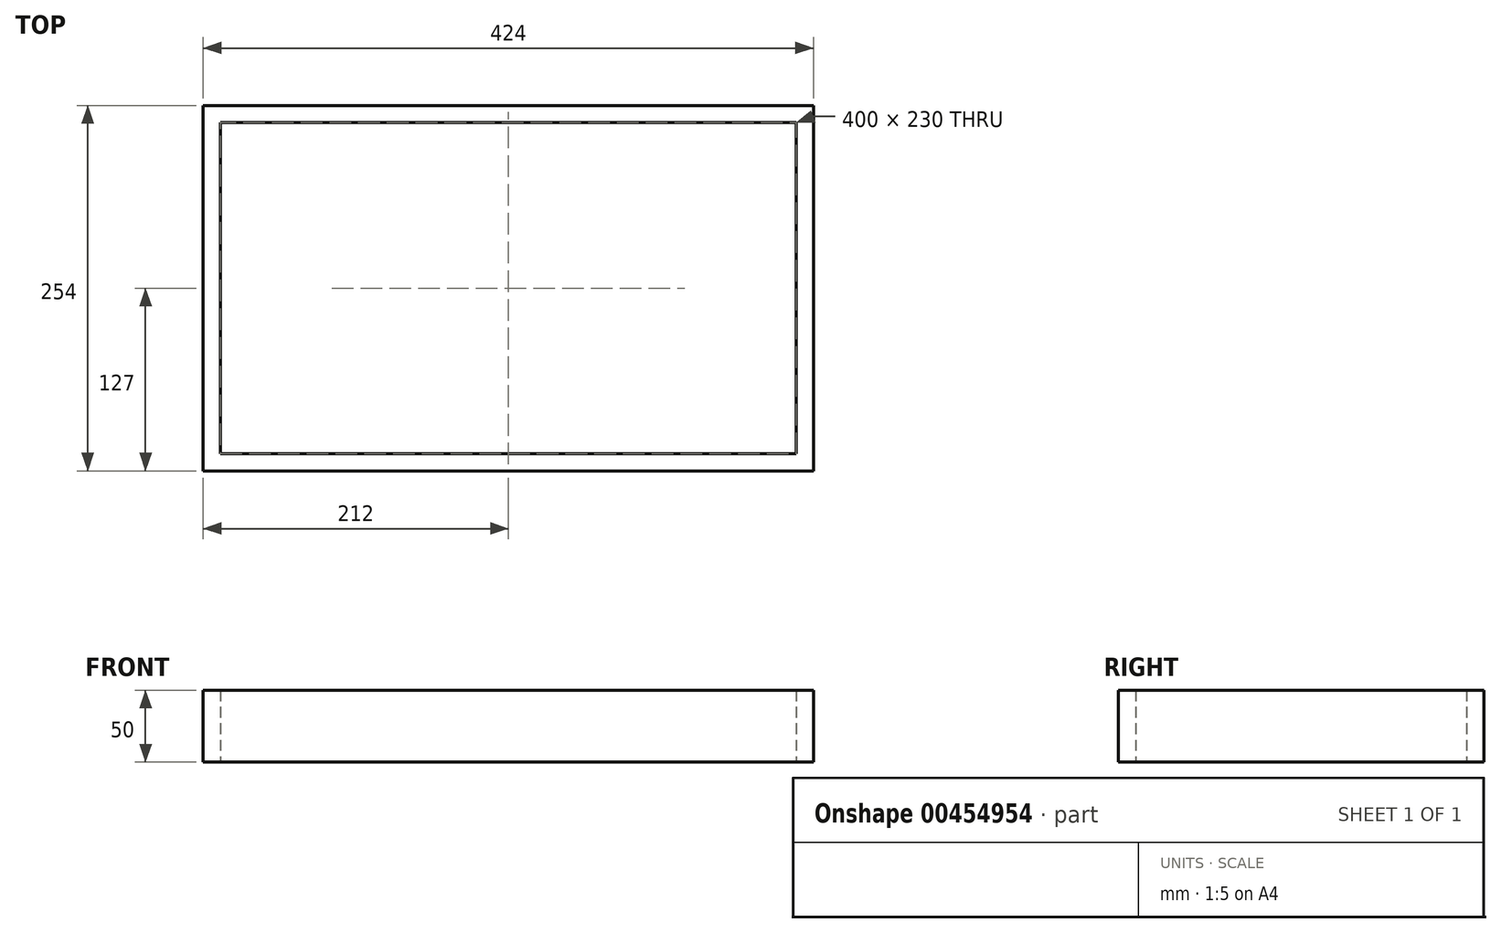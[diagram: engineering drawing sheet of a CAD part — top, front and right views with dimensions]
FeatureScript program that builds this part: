
annotation { "Feature Type Name" : "Feature", "Feature Type Description" : "" }
export const myFeature = defineFeature(function(context is Context, id is Id, definition is map)
    precondition{}
    {
        {
            var Q0;
            Q0=qCreatedBy(makeId("Top.planeOp"),FACE);
            var sketch = newSketch(context, id + "F0", { "sketchPlane" : qUnion([Q0])});
            skLineSegment(sketch, "E0.bottom", {"start": v(200, -115) * mm, "end": v(-200, -115) * mm});
            skLineSegment(sketch, "E0.top", {"start": v(200, 115) * mm, "end": v(-200, 115) * mm});
            skLineSegment(sketch, "E0.left", {"start": v(200, -115) * mm, "end": v(200, 115) * mm});
            skLineSegment(sketch, "E0.right", {"start": v(-200, -115) * mm, "end": v(-200, 115) * mm});
            skPoint(sketch, "E0.middle", {"position": v(0, 0) * mm});
            skLineSegment(sketch, "E1.bottom", {"start": v(212, -127) * mm, "end": v(-212, -127) * mm});
            skLineSegment(sketch, "E1.top", {"start": v(212, 127) * mm, "end": v(-212, 127) * mm});
            skLineSegment(sketch, "E1.left", {"start": v(212, -127) * mm, "end": v(212, 127) * mm});
            skLineSegment(sketch, "E1.right", {"start": v(-212, -127) * mm, "end": v(-212, 127) * mm});
            skSolve(sketch);
        }
        {
            var Q0;
            Q0 = qSketchRegion(id + "F0", true);
            extrude(context, id + "F1", {"entities" : qUnion([Q0]), "depth" : 50 * mm});
        }
    });
